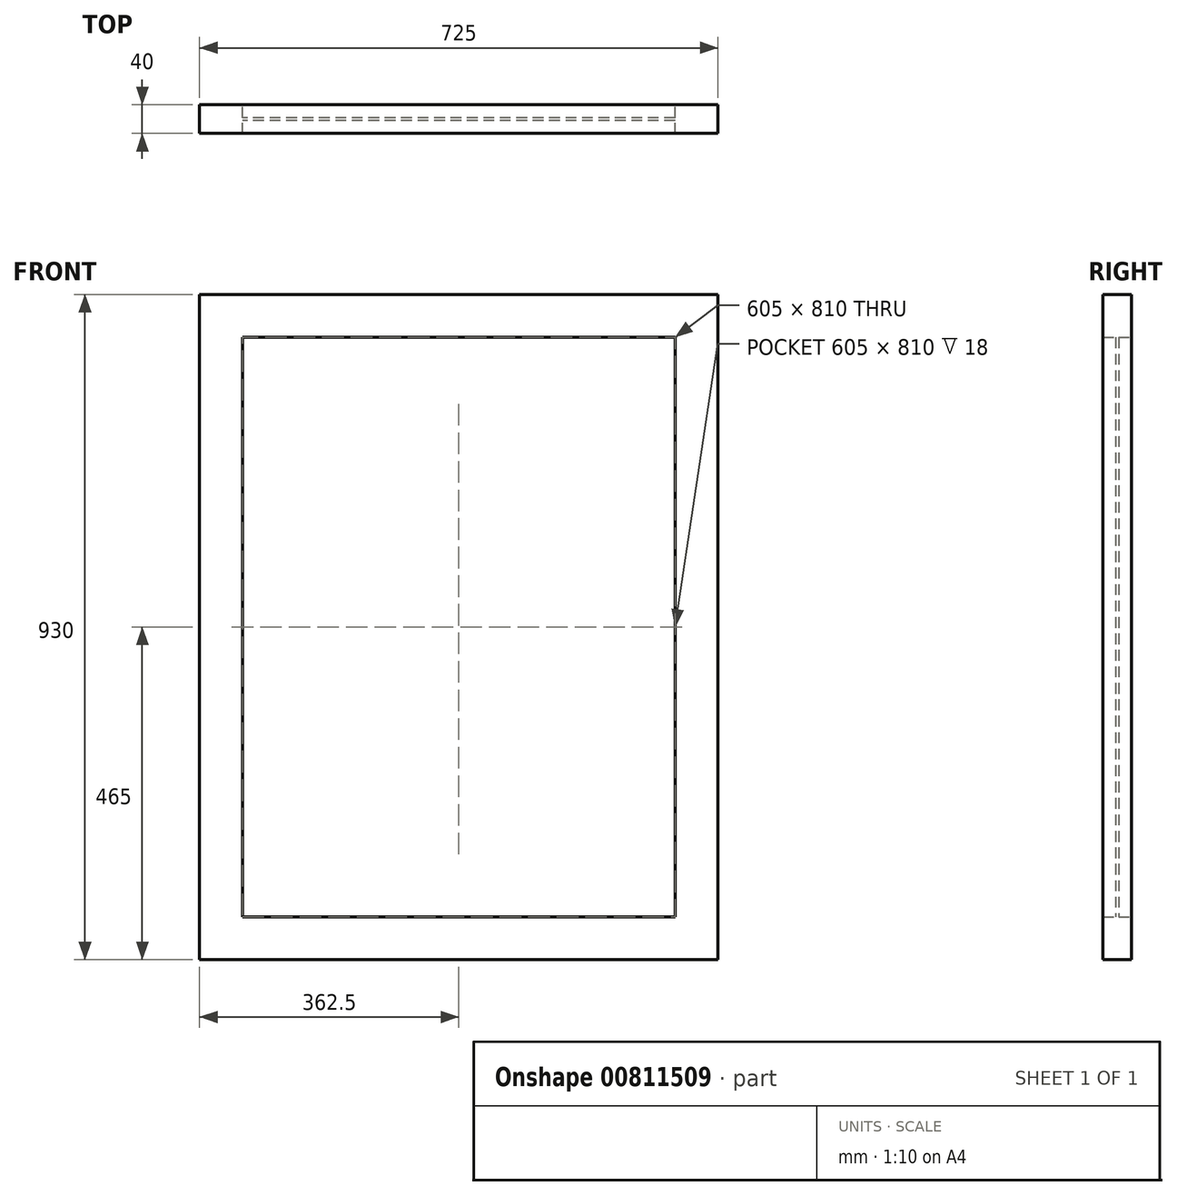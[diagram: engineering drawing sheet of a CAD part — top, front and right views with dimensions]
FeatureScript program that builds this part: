
annotation { "Feature Type Name" : "Feature", "Feature Type Description" : "" }
export const myFeature = defineFeature(function(context is Context, id is Id, definition is map)
    precondition{}
    {
        {
            var Q0;
            Q0=qCreatedBy(makeId("Front.planeOp"),FACE);
            var sketch = newSketch(context, id + "F0", { "sketchPlane" : qUnion([Q0])});
            skLineSegment(sketch, "E0.bottom", {"start": v(302.5, 405) * mm, "end": v(-302.5, 405) * mm});
            skLineSegment(sketch, "E0.top", {"start": v(302.5, -405) * mm, "end": v(-302.5, -405) * mm});
            skLineSegment(sketch, "E0.left", {"start": v(302.5, 405) * mm, "end": v(302.5, -405) * mm});
            skLineSegment(sketch, "E0.right", {"start": v(-302.5, 405) * mm, "end": v(-302.5, -405) * mm});
            skPoint(sketch, "E0.middle", {"position": v(0, 0) * mm});
            skLineSegment(sketch, "E1.bottom", {"start": v(362.5, 465) * mm, "end": v(-362.5, 465) * mm});
            skLineSegment(sketch, "E1.top", {"start": v(362.5, -465) * mm, "end": v(-362.5, -465) * mm});
            skLineSegment(sketch, "E1.left", {"start": v(362.5, 465) * mm, "end": v(362.5, -465) * mm});
            skLineSegment(sketch, "E1.right", {"start": v(-362.5, 465) * mm, "end": v(-362.5, -465) * mm});
            skSolve(sketch);
        }
        {
            var Q0;
            Q0=makeQuery(id+"F0.imprint","IMPRINT",FACE,{"disambiguationData":[TD([[makeQuery(id+"F0.imprint","IMPRINT",EDGE,{"derivedFrom":sQuery(id+"F0.wireOp",EDGE,"E0.bottom")}),-1.0]])]});
            extrude(context, id + "F1", {"entities" : qUnion([Q0]), "endBound" : BoundingType.SYMMETRIC, "depth" : 40 * mm, "offsetDistance" : 25 * mm});
        }
        {
            var Q0;
            Q0=makeQuery(id+"F0.imprint","IMPRINT",FACE,{"disambiguationData":[TD([[makeQuery(id+"F0.imprint","IMPRINT",EDGE,{"derivedFrom":sQuery(id+"F0.wireOp",EDGE,"E0.bottom")}),1.0]])]});
            extrude(context, id + "F2", {"entities" : qUnion([Q0]), "operationType" : NewBodyOperationType.ADD, "endBound" : BoundingType.SYMMETRIC, "depth" : 4 * mm, "offsetDistance" : 25 * mm});
        }
    });
